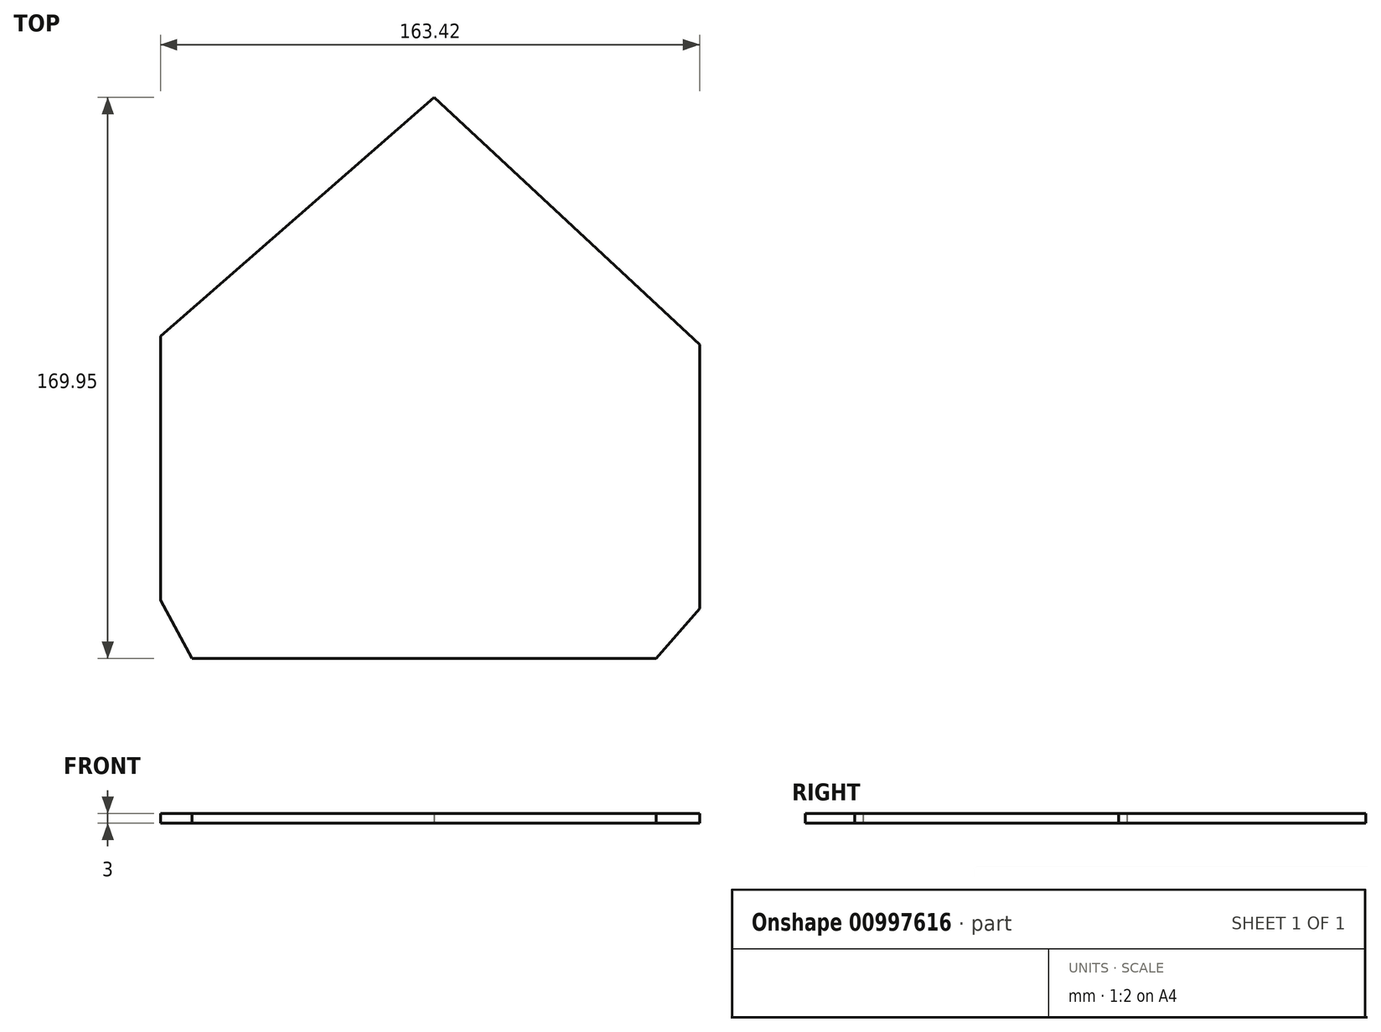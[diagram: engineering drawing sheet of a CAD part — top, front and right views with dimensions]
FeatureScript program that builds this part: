
annotation { "Feature Type Name" : "Feature", "Feature Type Description" : "" }
export const myFeature = defineFeature(function(context is Context, id is Id, definition is map)
    precondition{}
    {
        {
            var Q0;
            Q0=qCreatedBy(makeId("Top.planeOp"),FACE);
            var sketch = newSketch(context, id + "F0", { "sketchPlane" : qUnion([Q0])});
            skLineSegment(sketch, "E0", {"start": v(-84.32, 0) * mm, "end": v(-84.32, -80) * mm});
            skLineSegment(sketch, "E1", {"start": v(-84.32, -80) * mm, "end": v(-74.84, -97.61) * mm});
            skLineSegment(sketch, "E2", {"start": v(-74.84, -97.61) * mm, "end": v(65.93, -97.61) * mm});
            skLineSegment(sketch, "E3", {"start": v(65.93, -97.61) * mm, "end": v(79.1, -82.56) * mm});
            skLineSegment(sketch, "E4", {"start": v(79.1, -82.56) * mm, "end": v(79.1, -2.56) * mm});
            skLineSegment(sketch, "E5", {"start": v(-84.32, 0) * mm, "end": v(-1.45, 72.34) * mm});
            skLineSegment(sketch, "E6", {"start": v(-1.45, 72.34) * mm, "end": v(79.1, -2.56) * mm});
            skSolve(sketch);
        }
        {
            var Q0;
            Q0=makeQuery(id+"F0.imprint","IMPRINT",FACE,{"disambiguationData":[TD([[makeQuery(id+"F0.imprint","IMPRINT",EDGE,{"derivedFrom":sQuery(id+"F0.wireOp",EDGE,"E0")}),1.0]])]});
            extrude(context, id + "F1", {"entities" : qUnion([Q0]), "depth" : 3 * mm, "offsetDistance" : 25 * mm});
        }
    });
